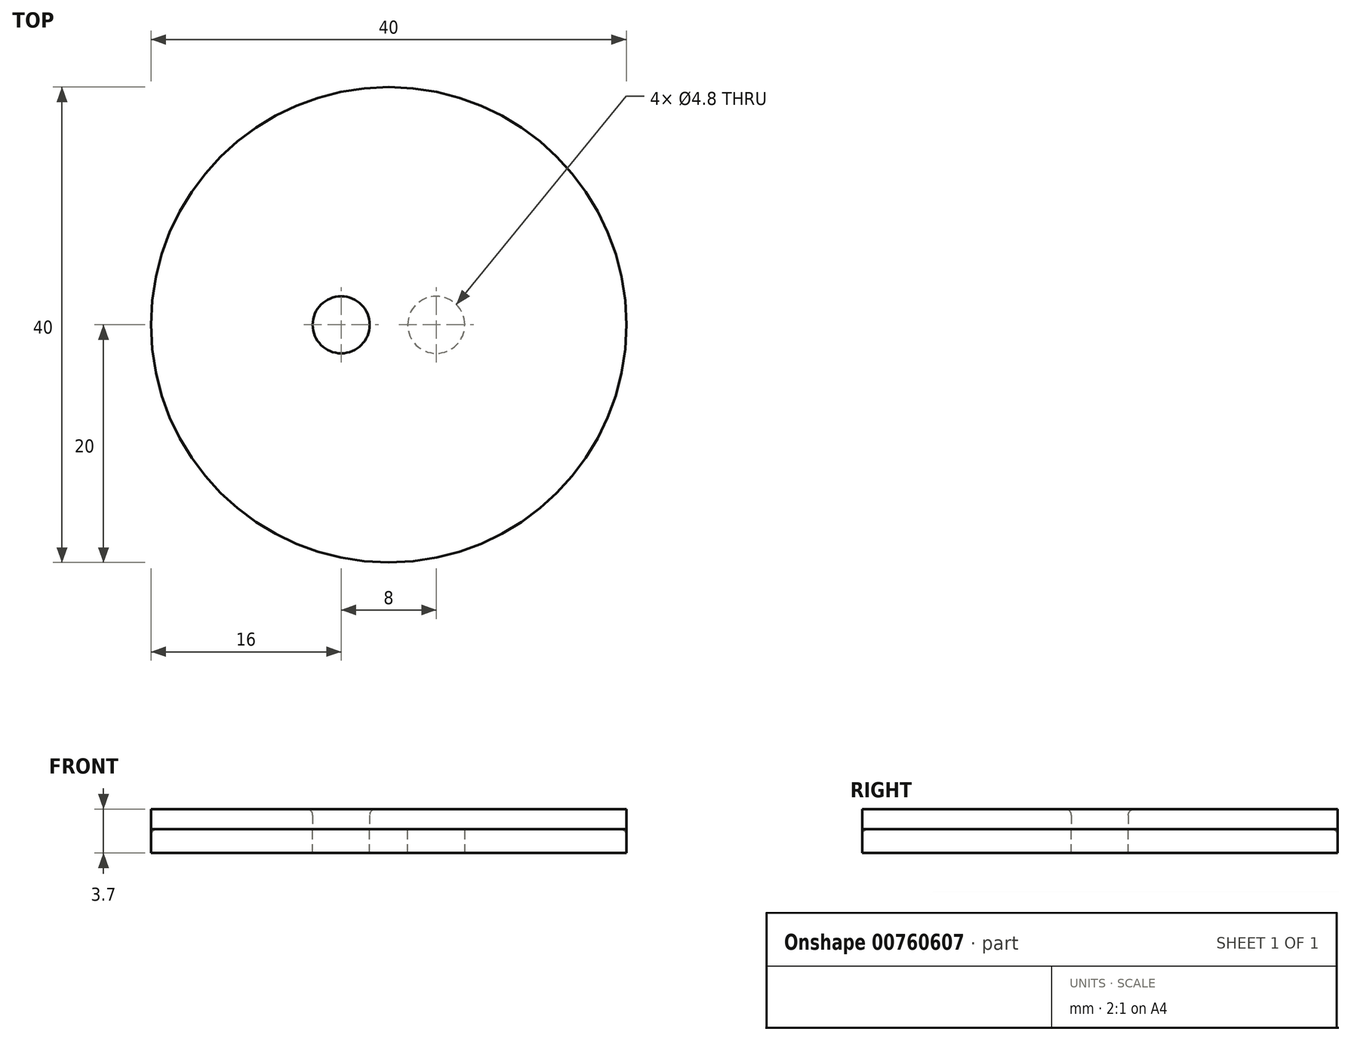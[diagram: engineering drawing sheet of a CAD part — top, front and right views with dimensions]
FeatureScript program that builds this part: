
annotation { "Feature Type Name" : "Feature", "Feature Type Description" : "" }
export const myFeature = defineFeature(function(context is Context, id is Id, definition is map)
    precondition{}
    {
        {
            var Q0;
            Q0=qCreatedBy(makeId("Top.planeOp"),FACE);
            var sketch = newSketch(context, id + "F0", { "sketchPlane" : qUnion([Q0])});
            skCircle(sketch, "E0", {"center": v(0, 0) * mm, "radius": 20 * mm});
            skCircle(sketch, "E1", {"center": v(4, 0) * mm, "radius": 2.4 * mm});
            skLineSegment(sketch, "E2", {"start": v(0, 0) * mm, "end": v(0, 2.54) * mm, "construction": true});
            skCircle(sketch, "E3.MirrorC", {"center": v(-4, 0) * mm, "radius": 2.4 * mm});
            skSolve(sketch);
        }
        {
            var Q0;
            Q0=makeQuery(id+"F0.imprint","IMPRINT",FACE,{"disambiguationData":[TD([[makeQuery(id+"F0.imprint","IMPRINT",EDGE,{"derivedFrom":sQuery(id+"F0.wireOp",EDGE,"E3.MirrorC")}),-1.0]])]});
            var Q1;
            Q1=makeQuery(id+"F0.imprint","IMPRINT",FACE,{"disambiguationData":[TD([[makeQuery(id+"F0.imprint","IMPRINT",EDGE,{"derivedFrom":sQuery(id+"F0.wireOp",EDGE,"E1")}),1.0]])]});
            extrude(context, id + "F1", {"entities" : qUnion([Q0, Q1]), "depth" : 1.7 * mm, "offsetDistance" : 25 * mm});
        }
        {
            var Q0;
            Q0 = qSketchRegion(id + "F0", true);
            extrude(context, id + "F2", {"entities" : qUnion([Q0]), "oppositeDirection" : true, "depth" : 2 * mm, "offsetDistance" : 25 * mm});
        }
        {
            var Q0;
            Q0=makeQuery(id+"F1.opExtrude","CAP_EDGE",EDGE,{"disambiguationData":[OSD([sQuery(id+"F0.wireOp",EDGE,"E3.MirrorC")])],"isStart":false});
            var Q1;
            Q1=makeQuery(id+"F1.opExtrude","CAP_EDGE",EDGE,{"disambiguationData":[OSD([sQuery(id+"F0.wireOp",EDGE,"E1")])],"isStart":false});
            var Q2;
            Q2=makeQuery(id+"F2.opExtrude","CAP_EDGE",EDGE,{"disambiguationData":[OSD([sQuery(id+"F0.wireOp",EDGE,"E0")])],"isStart":true});
            fillet(context, id + "F3", {"entities" : qUnion([Q0, Q1, Q2]), "radius" : 0.5 * mm, "tangentPropagation" : true, "allowEdgeOverflow" : false});
        }
        {
            var Q0;
            Q0=makeQuery(id+"F1.opExtrude","CAP_FACE",FACE,{"disambiguationData":[OSD([sQuery(id+"F0.wireOp",EDGE,"E3.MirrorC")])],"isStart":true});
            var Q1;
            Q1=makeQuery(id+"F1.opExtrude","CAP_FACE",FACE,{"disambiguationData":[OSD([sQuery(id+"F0.wireOp",EDGE,"E1")])],"isStart":true});
            extrude(context, id + "F4", {"entities" : qUnion([Q0, Q1]), "depth" : 2 * mm, "offsetDistance" : 25 * mm});
        }
    });
